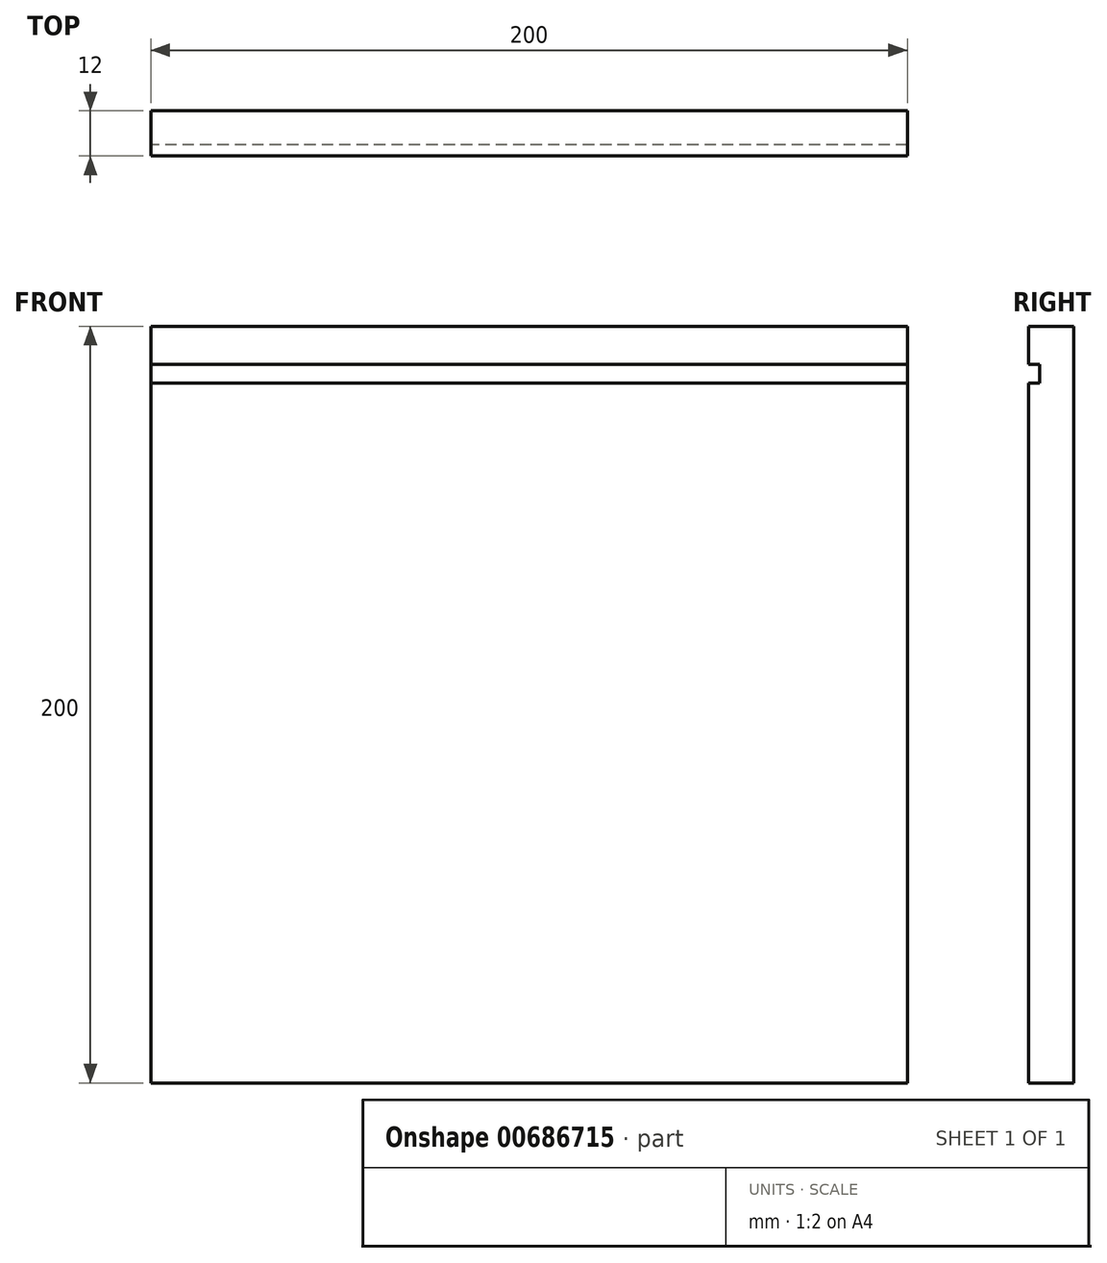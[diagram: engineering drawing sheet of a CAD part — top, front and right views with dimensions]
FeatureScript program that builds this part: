
annotation { "Feature Type Name" : "Feature", "Feature Type Description" : "" }
export const myFeature = defineFeature(function(context is Context, id is Id, definition is map)
    precondition{}
    {
        {
            var Q0;
            Q0=qCreatedBy(makeId("Right.planeOp"),FACE);
            var sketch = newSketch(context, id + "F0", { "sketchPlane" : qUnion([Q0])});
            skLineSegment(sketch, "E0.bottom", {"start": v(0, 0) * mm, "end": v(12, 0) * mm});
            skLineSegment(sketch, "E0.top", {"start": v(0, 200) * mm, "end": v(12, 200) * mm});
            skLineSegment(sketch, "E0.left", {"start": v(0, 0) * mm, "end": v(0, 185) * mm});
            skLineSegment(sketch, "E0.right", {"start": v(12, 0) * mm, "end": v(12, 200) * mm});
            skLineSegment(sketch, "E1.bottom", {"start": v(0, 190) * mm, "end": v(3, 190) * mm});
            skLineSegment(sketch, "E1.top", {"start": v(0, 185) * mm, "end": v(3, 185) * mm});
            skLineSegment(sketch, "E1.right", {"start": v(3, 190) * mm, "end": v(3, 185) * mm});
            skLineSegment(sketch, "E2.trimOffspring", {"start": v(0, 190) * mm, "end": v(0, 200) * mm});
            skSolve(sketch);
        }
        {
            var Q0;
            Q0=qSketchRegion(id+"F0",true);
            extrude(context, id + "F1", {"entities" : qUnion([Q0]), "depth" : 200 * mm, "offsetDistance" : 25 * mm});
        }
    });
